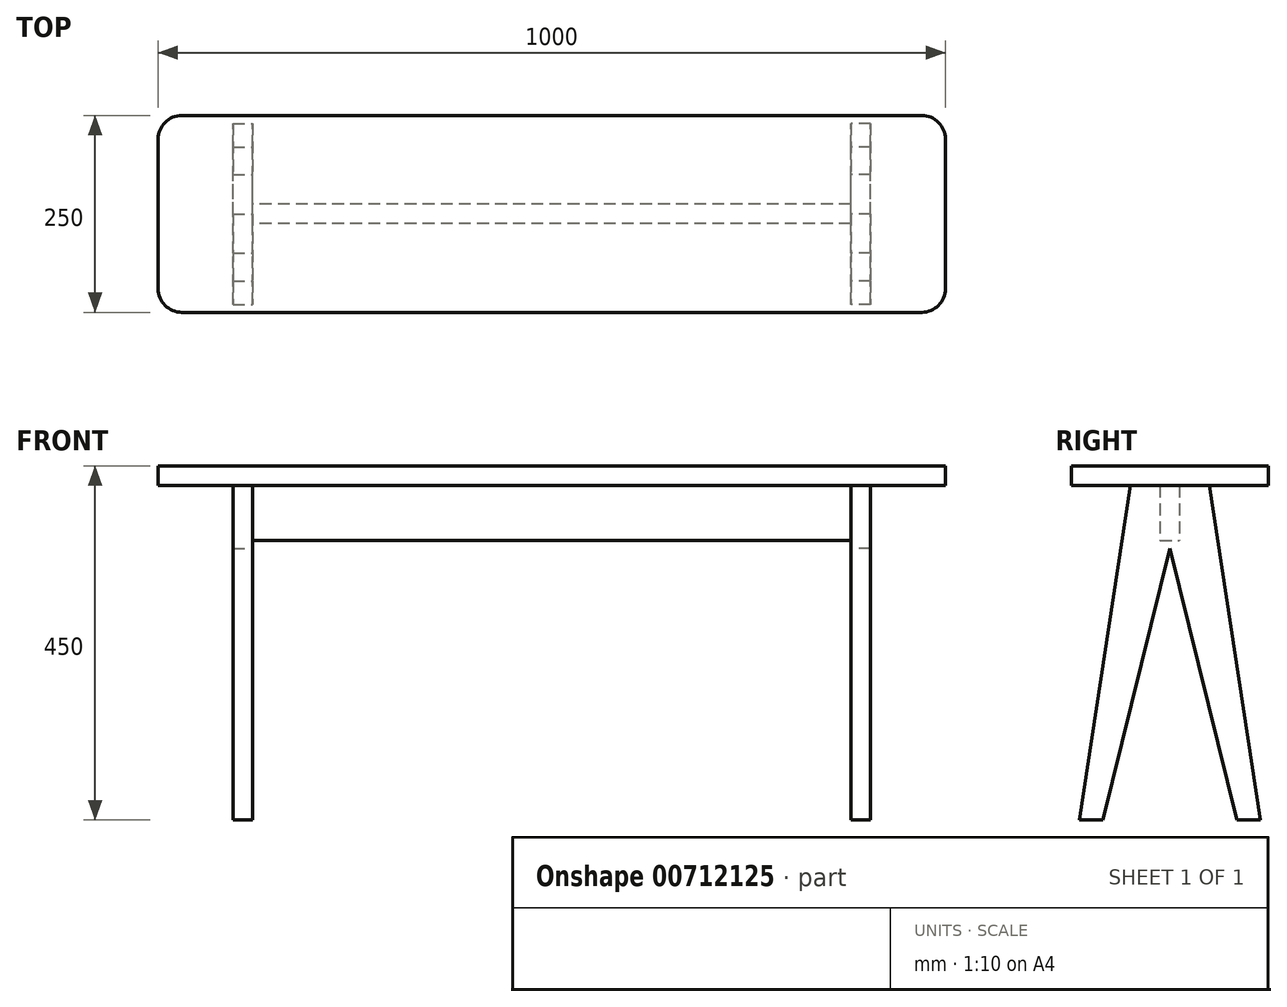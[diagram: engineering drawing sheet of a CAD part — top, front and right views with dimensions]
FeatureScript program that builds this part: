
annotation { "Feature Type Name" : "Feature", "Feature Type Description" : "" }
export const myFeature = defineFeature(function(context is Context, id is Id, definition is map)
    precondition{}
    {
        {
            var Q0;
            Q0=qCreatedBy(makeId("Top.planeOp"),FACE);
            var sketch = newSketch(context, id + "F0", { "sketchPlane" : qUnion([Q0])});
            skLineSegment(sketch, "E0.bottom", {"start": v(-500, 125) * mm, "end": v(500, 125) * mm});
            skLineSegment(sketch, "E0.top", {"start": v(-500, -125) * mm, "end": v(500, -125) * mm});
            skLineSegment(sketch, "E0.left", {"start": v(-500, 125) * mm, "end": v(-500, -125) * mm});
            skLineSegment(sketch, "E0.right", {"start": v(500, 125) * mm, "end": v(500, -125) * mm});
            skPoint(sketch, "E0.middle", {"position": v(0, 0) * mm});
            skSolve(sketch);
        }
        {
            var Q0;
            Q0 = qSketchRegion(id + "F0", true);
            extrude(context, id + "F1", {"entities" : qUnion([Q0]), "depth" : 25 * mm, "offsetDistance" : 25 * mm});
        }
        {
            var Q0;
            Q0=qCreatedBy(makeId("Front.planeOp"),FACE);
            var sketch = newSketch(context, id + "F2", { "sketchPlane" : qUnion([Q0])});
            skLineSegment(sketch, "E1.bottom", {"start": v(0, 0) * mm, "end": v(-380, 0) * mm});
            skLineSegment(sketch, "E1.top", {"start": v(0, -70) * mm, "end": v(-380, -70) * mm});
            skLineSegment(sketch, "E1.left", {"start": v(0, 0) * mm, "end": v(0, -70) * mm});
            skLineSegment(sketch, "E1.right", {"start": v(-380, 0) * mm, "end": v(-380, -70) * mm});
            skLineSegment(sketch, "E2", {"start": v(0, 61.34) * mm, "end": v(0, -77.84) * mm});
            skLineSegment(sketch, "E3.MirrorCS", {"start": v(0, -70) * mm, "end": v(380, -70) * mm});
            skLineSegment(sketch, "E4.MirrorCS", {"start": v(380, 0) * mm, "end": v(380, -70) * mm});
            skLineSegment(sketch, "E5.MirrorCS", {"start": v(0, 0) * mm, "end": v(380, 0) * mm});
            skSolve(sketch);
        }
        {
            var Q0;
            Q0 = qSketchRegion(id + "F2", true);
            extrude(context, id + "F3", {"entities" : qUnion([Q0]), "operationType" : NewBodyOperationType.ADD, "endBound" : BoundingType.SYMMETRIC, "depth" : 25 * mm, "offsetDistance" : 25 * mm});
        }
        {
            var Q0;
            Q0=qCreatedBy(makeId("Right.planeOp"),FACE);
            var sketch = newSketch(context, id + "F4", { "sketchPlane" : qUnion([Q0])});
            skLineSegment(sketch, "E6", {"start": v(0, 44.48) * mm, "end": v(0, -111.8) * mm});
            skLineSegment(sketch, "E7", {"start": v(0, -80) * mm, "end": v(-85, -425) * mm});
            skLineSegment(sketch, "E8", {"start": v(-85, -425) * mm, "end": v(-115, -425) * mm});
            skLineSegment(sketch, "E9", {"start": v(-115, -425) * mm, "end": v(-50, 0) * mm});
            skLineSegment(sketch, "E10", {"start": v(-50, 0) * mm, "end": v(0, 0) * mm});
            skLineSegment(sketch, "E11.MirrorCS", {"start": v(50, 0) * mm, "end": v(0, 0) * mm});
            skLineSegment(sketch, "E12.MirrorCS", {"start": v(115, -425) * mm, "end": v(50, 0) * mm});
            skLineSegment(sketch, "E13.MirrorCS", {"start": v(85, -425) * mm, "end": v(115, -425) * mm});
            skLineSegment(sketch, "E14.MirrorCS", {"start": v(0, -80) * mm, "end": v(85, -425) * mm});
            skSolve(sketch);
        }
        {
            var Q0;
            Q0 = qSketchRegion(id + "F4", true);
            extrude(context, id + "F5", {"entities" : qUnion([Q0]), "operationType" : NewBodyOperationType.ADD, "depth" : 405 * mm, "offsetDistance" : 25 * mm, "hasSecondDirection" : true, "secondDirectionOppositeDirection" : false, "secondDirectionDepth" : 380 * mm});
        }
        {
            var Q0;
            {var subQ0=sQuery(id+"F4.wireOp",EDGE,"E7");Q0=makeQuery(id+"F4.imprint","IMPRINT",FACE,{"disambiguationData":[TD([[makeQuery(id+"F4.imprint","IMPRINT",EDGE,{"derivedFrom":subQ0}),-1.0]])]});}
            var Q1;
            {var subQ0=sQuery(id+"F4.wireOp",EDGE,"E11.MirrorCS");Q1=makeQuery(id+"F4.imprint","IMPRINT",FACE,{"disambiguationData":[TD([[makeQuery(id+"F4.imprint","IMPRINT",EDGE,{"derivedFrom":subQ0}),1.0]])]});}
            extrude(context, id + "F6", {"entities" : qUnion([Q0, Q1]), "operationType" : NewBodyOperationType.ADD, "oppositeDirection" : true, "depth" : 405 * mm, "offsetDistance" : 25 * mm, "hasSecondDirection" : true, "secondDirectionOppositeDirection" : true, "secondDirectionDepth" : 380 * mm});
        }
        {
            var Q0;
            Q0=makeQuery(id+"F1.opExtrude","SWEPT_EDGE",EDGE,{"disambiguationData":[OSD([sQuery(id+"F0.wireOp",EDGE,"E0.bottom"),sQuery(id+"F0.wireOp",EDGE,"E0.right")])]});
            var Q1;
            Q1=makeQuery(id+"F1.opExtrude","SWEPT_EDGE",EDGE,{"disambiguationData":[OSD([sQuery(id+"F0.wireOp",EDGE,"E0.top"),sQuery(id+"F0.wireOp",EDGE,"E0.right")])]});
            var Q2;
            Q2=makeQuery(id+"F1.opExtrude","SWEPT_EDGE",EDGE,{"disambiguationData":[OSD([sQuery(id+"F0.wireOp",EDGE,"E0.bottom"),sQuery(id+"F0.wireOp",EDGE,"E0.left")])]});
            var Q3;
            Q3=makeQuery(id+"F1.opExtrude","SWEPT_EDGE",EDGE,{"disambiguationData":[OSD([sQuery(id+"F0.wireOp",EDGE,"E0.top"),sQuery(id+"F0.wireOp",EDGE,"E0.left")])]});
            fillet(context, id + "F7", {"entities" : qUnion([Q0, Q1, Q2, Q3]), "radius" : 30 * mm, "tangentPropagation" : true, "allowEdgeOverflow" : false});
        }
    });
